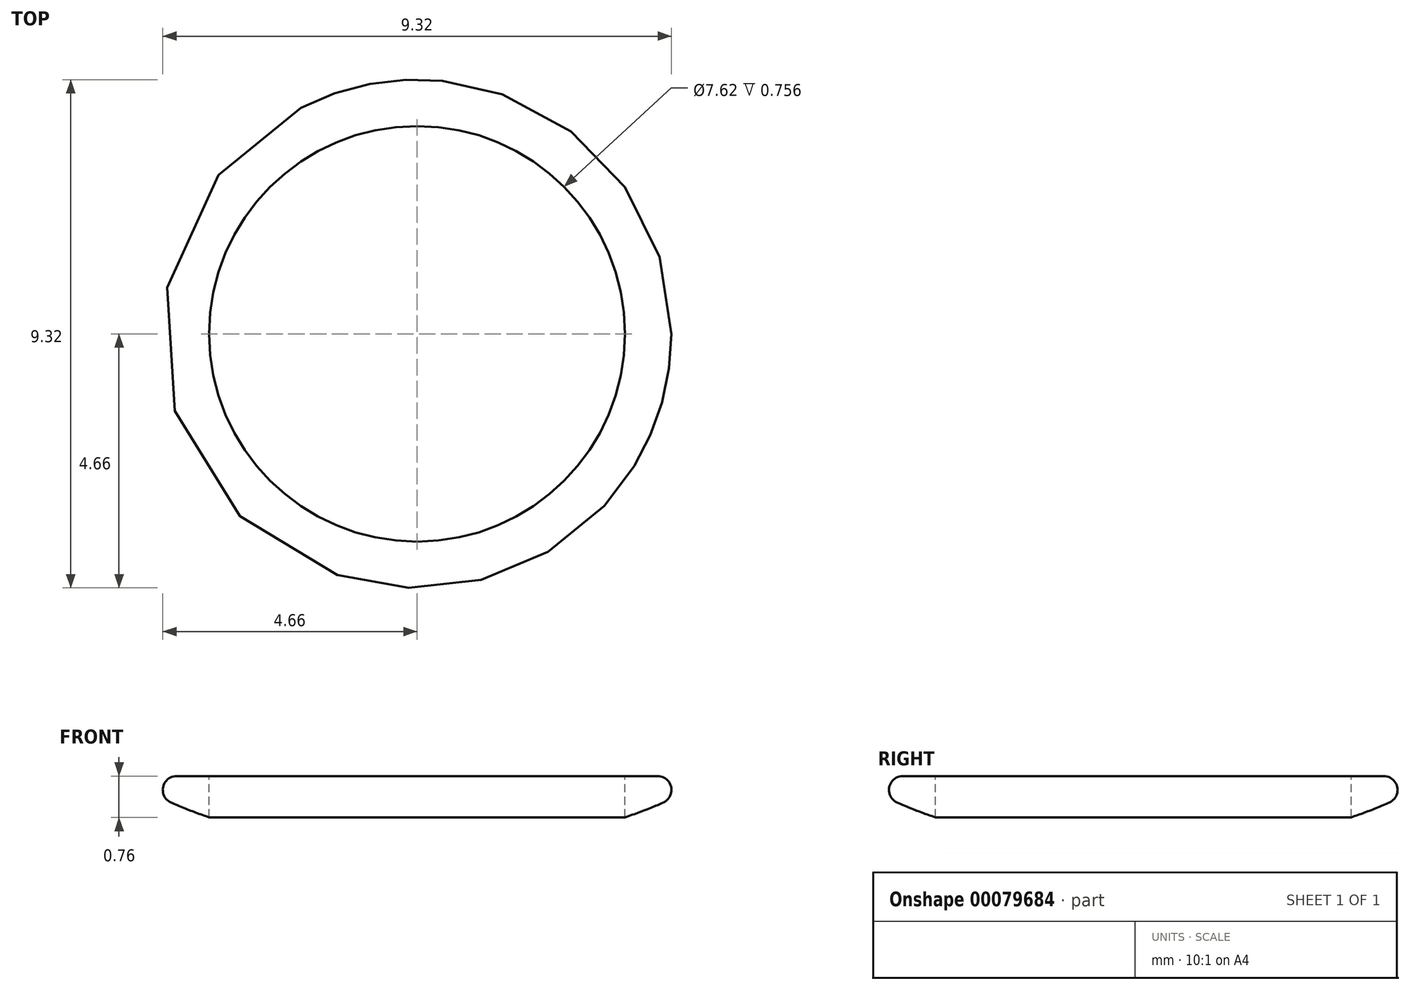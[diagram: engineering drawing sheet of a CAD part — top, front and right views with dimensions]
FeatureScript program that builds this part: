
annotation { "Feature Type Name" : "Feature", "Feature Type Description" : "" }
export const myFeature = defineFeature(function(context is Context, id is Id, definition is map)
    precondition{}
    {
        {
            var Q0;
            Q0=qCreatedBy(makeId("Top.planeOp"),FACE);
            var sketch = newSketch(context, id + "F0", { "sketchPlane" : qUnion([Q0])});
            skCircle(sketch, "E0", {"center": v(0, 0) * mm, "radius": 1.27 * mm});
            skPoint(sketch, "E1", {"position": v(1.27, 0) * mm});
            skSolve(sketch);
        }
        {
            var Q0;
            Q0 = qSketchRegion(id + "F0", true);
            extrude(context, id + "F1", {"entities" : qUnion([Q0]), "depth" : 5.08 * mm});
        }
        {
            var Q0;
            Q0=qCreatedBy(makeId("Right.planeOp"),FACE);
            var sketch = newSketch(context, id + "F2", { "sketchPlane" : qUnion([Q0])});
            skPoint(sketch, "E2", {"position": v(-1.27, 0) * mm});
            skPoint(sketch, "E3", {"position": v(0, 5.08) * mm});
            skPoint(sketch, "E4", {"position": v(-1.27, 3.81) * mm});
            skPoint(sketch, "E5.1.internal.orphan", {"position": v(-6.12, 5.08) * mm});
            skPoint(sketch, "E5.2.internal.orphan", {"position": v(-6.1, 5.08) * mm});
            skFitSpline(sketch, "E6", {"points": [v(-1.27, 3.81) * mm, v(-5.08, 5.08) * mm, v(-0.06, 6.25) * mm, v(-1.43, 9.03) * mm], "startDerivative": vector(-13.13, 0.17) * mm, "endDerivative": vector(0.25, -1.46) * mm});
            skLineSegment(sketch, "E7", {"start": v(-5.08, 5.08) * mm, "end": v(0, 5.08) * mm});
            skLineSegment(sketch, "E8", {"start": v(-1.27, 3.81) * mm, "end": v(-1.27, 5.08) * mm});
            skLineSegment(sketch, "E9", {"start": v(0, 5.08) * mm, "end": v(0, 0) * mm, "construction": true});
            skSolve(sketch);
        }
        {
            var Q0;
            {var subQ0=sQuery(id+"F2.wireOp",EDGE,"E6");Q0=makeQuery(id+"F2.imprint","IMPRINT",FACE,{"disambiguationData":[TD([[makeQuery(id+"F2.imprint","IMPRINT",EDGE,{"derivedFrom":subQ0}),-1.0]])]});}
            var Q1;
            Q1=sQuery(id+"F2.wireOp",EDGE,"E9");
            revolve(context, id + "F3", {"operationType" : NewBodyOperationType.ADD, "entities" : qUnion([Q0]), "axis" : qUnion([Q1]), "revolveType" : RevolveType.FULL});
        }
        {
            var Q0;
            Q0=makeQuery(id+"F3.opRevolve","SWEPT_EDGE",EDGE,{"disambiguationData":[OSD([sQuery(id+"F2.wireOp",EDGE,"E6"),sQuery(id+"F2.wireOp",EDGE,"E7")])]});
            fillet(context, id + "F4", {"entities" : qUnion([Q0]), "radius" : 0.25 * mm, "tangentPropagation" : true, "allowEdgeOverflow" : false});
        }
        {
            var Q0;
            Q0=makeQuery(id+"F3.boolean.opBoolean","MERGE",FACE,{"derivedFrom":[makeQuery(id+"F1.opExtrude","CAP_FACE",FACE,{"disambiguationData":[OSD([sQuery(id+"F0.wireOp",EDGE,"E0")])],"isStart":false}),makeQuery(id+"F3.opRevolve","SWEPT_FACE",FACE,{"disambiguationData":[OSD([sQuery(id+"F2.wireOp",EDGE,"E7")])]})]});
            var sketch = newSketch(context, id + "F5", { "sketchPlane" : qUnion([Q0])});
            skCircle(sketch, "E10", {"center": v(0, 0) * mm, "radius": 3.81 * mm, "construction": true});
            skLineSegment(sketch, "E11", {"start": v(0, 0) * mm, "end": v(-1.27, 3.6) * mm});
            skLineSegment(sketch, "E12", {"start": v(0, 0) * mm, "end": v(1.27, 3.6) * mm});
            skLineSegment(sketch, "E13", {"start": v(0, 0) * mm, "end": v(0, 3.81) * mm, "construction": true});
            skLineSegment(sketch, "E14.1.0", {"start": v(0, 0) * mm, "end": v(-3.02, 2.32) * mm});
            skLineSegment(sketch, "E14.1.1", {"start": v(0, 0) * mm, "end": v(-3.8, -0.1) * mm});
            skLineSegment(sketch, "E14.2.0", {"start": v(0, 0) * mm, "end": v(-3.14, -2.16) * mm});
            skLineSegment(sketch, "E14.2.1", {"start": v(0, 0) * mm, "end": v(-1.08, -3.65) * mm});
            skLineSegment(sketch, "E14.3.0", {"start": v(0, 0) * mm, "end": v(1.08, -3.65) * mm});
            skLineSegment(sketch, "E14.3.1", {"start": v(0, 0) * mm, "end": v(3.14, -2.16) * mm});
            skLineSegment(sketch, "E14.4.0", {"start": v(0, 0) * mm, "end": v(3.8, -0.1) * mm});
            skLineSegment(sketch, "E14.4.1", {"start": v(0, 0) * mm, "end": v(3.02, 2.32) * mm});
            skCircle(sketch, "E15", {"center": v(0, 0) * mm, "radius": 3.81 * mm});
            skSolve(sketch);
        }
        {
            var Q0;
            Q0 = qSketchRegion(id + "F5", true);
            extrude(context, id + "F6", {"entities" : qUnion([Q0]), "operationType" : NewBodyOperationType.REMOVE, "oppositeDirection" : true, "depth" : 25.4 * mm});
        }
    });
